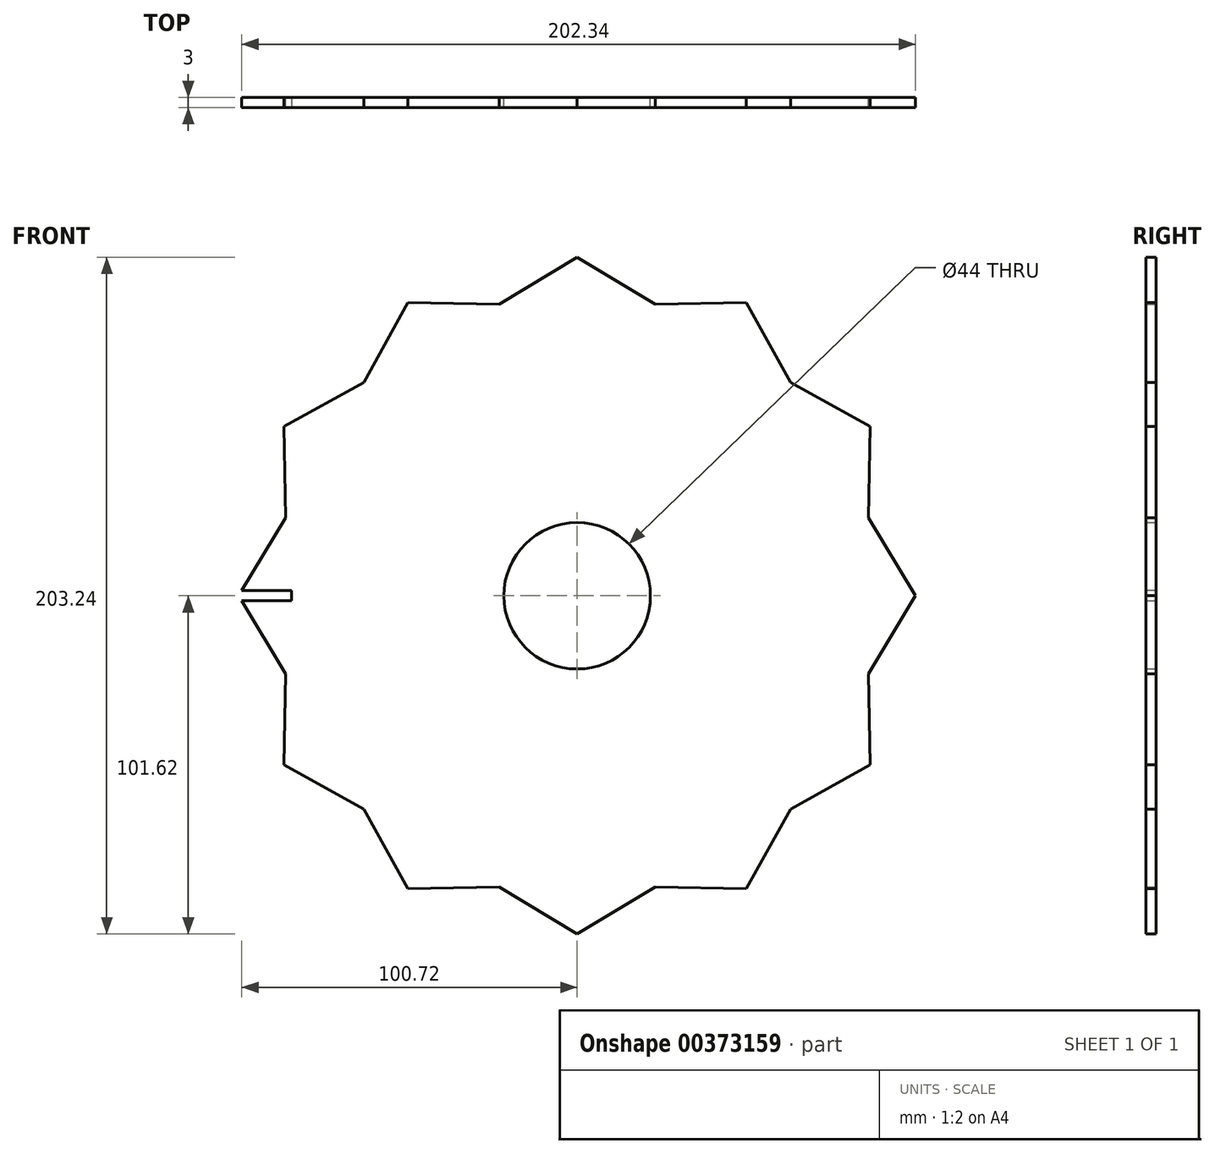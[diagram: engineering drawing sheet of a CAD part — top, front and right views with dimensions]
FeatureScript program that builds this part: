
annotation { "Feature Type Name" : "Feature", "Feature Type Description" : "" }
export const myFeature = defineFeature(function(context is Context, id is Id, definition is map)
    precondition{}
    {
        {
            var Q0;
            Q0=qCreatedBy(makeId("Front.planeOp"),FACE);
            var sketch = newSketch(context, id + "F0", { "sketchPlane" : qUnion([Q0])});
            skCircle(sketch, "E0", {"center": v(0, 0) * mm, "radius": 22 * mm});
            skLineSegment(sketch, "E1", {"start": v(-23.45, 87.53) * mm, "end": v(0, 101.62) * mm});
            skLineSegment(sketch, "E2", {"start": v(0, 101.62) * mm, "end": v(0, 56.8) * mm});
            skLineSegment(sketch, "E3.MirrorCS", {"start": v(23.45, 87.53) * mm, "end": v(0, 101.62) * mm});
            skLineSegment(sketch, "E4.1.0", {"start": v(-64.08, 64.08) * mm, "end": v(-50.81, 88) * mm});
            skLineSegment(sketch, "E4.1.1", {"start": v(-23.45, 87.53) * mm, "end": v(-50.81, 88) * mm});
            skLineSegment(sketch, "E4.2.0", {"start": v(-87.53, 23.45) * mm, "end": v(-88, 50.81) * mm});
            skLineSegment(sketch, "E4.2.1", {"start": v(-64.08, 64.08) * mm, "end": v(-88, 50.81) * mm});
            skLineSegment(sketch, "E4.3.0", {"start": v(-87.53, -23.45) * mm, "end": v(-101.62, 0) * mm});
            skLineSegment(sketch, "E4.3.1", {"start": v(-87.53, 23.45) * mm, "end": v(-101.62, 0) * mm});
            skLineSegment(sketch, "E4.4.1", {"start": v(-87.53, -23.45) * mm, "end": v(-88, -50.81) * mm});
            skLineSegment(sketch, "E4.5.0", {"start": v(-23.45, -87.53) * mm, "end": v(-50.81, -88) * mm});
            skLineSegment(sketch, "E4.5.1", {"start": v(-64.08, -64.08) * mm, "end": v(-50.81, -88) * mm});
            skLineSegment(sketch, "E4.6.0", {"start": v(23.45, -87.53) * mm, "end": v(0, -101.62) * mm});
            skLineSegment(sketch, "E4.6.1", {"start": v(-23.45, -87.53) * mm, "end": v(0, -101.62) * mm});
            skLineSegment(sketch, "E4.7.0", {"start": v(64.08, -64.08) * mm, "end": v(50.81, -88) * mm});
            skLineSegment(sketch, "E4.9.0", {"start": v(87.53, 23.45) * mm, "end": v(101.62, 0) * mm});
            skLineSegment(sketch, "E4.10.0", {"start": v(64.08, 64.08) * mm, "end": v(88, 50.81) * mm});
            skLineSegment(sketch, "E4.11.0", {"start": v(23.45, 87.53) * mm, "end": v(50.81, 88) * mm});
            skLineSegment(sketch, "E4.11.1", {"start": v(64.08, 64.08) * mm, "end": v(50.81, 88) * mm});
            skPoint(sketch, "E5.orphan", {"position": v(65.57, -60) * mm});
            skPoint(sketch, "E6.orphan", {"position": v(56.78, -32.78) * mm});
            skPoint(sketch, "E7.orphan", {"position": v(60, -65.57) * mm});
            skLineSegment(sketch, "E8.trimOffspring", {"start": v(64.08, -64.08) * mm, "end": v(88, -50.81) * mm});
            skPoint(sketch, "E9.orphan", {"position": v(84.75, -26.78) * mm});
            skLineSegment(sketch, "E10.trimOffspring", {"start": v(87.53, -23.45) * mm, "end": v(101.62, 0) * mm});
            skPoint(sketch, "E11.orphan", {"position": v(86.78, -19.18) * mm});
            skPoint(sketch, "E12.orphan", {"position": v(86.78, 19.18) * mm});
            skLineSegment(sketch, "E13.trimOffspring", {"start": v(87.53, 23.45) * mm, "end": v(88, 50.81) * mm});
            skPoint(sketch, "E14.orphan", {"position": v(65.57, 60) * mm});
            skPoint(sketch, "E15.orphan", {"position": v(84.75, 26.78) * mm});
            skPoint(sketch, "E16.orphan", {"position": v(56.78, 32.78) * mm});
            skPoint(sketch, "E17.orphan", {"position": v(60, 65.57) * mm});
            skPoint(sketch, "E18.MirrorCS.start.orphan", {"position": v(0, 65.57) * mm});
            skPoint(sketch, "E19.orphan", {"position": v(26.78, 84.75) * mm});
            skPoint(sketch, "E20.orphan", {"position": v(19.18, 86.78) * mm});
            skPoint(sketch, "E21.orphan", {"position": v(-19.18, 86.78) * mm});
            skPoint(sketch, "E22.orphan", {"position": v(-26.78, 84.75) * mm});
            skPoint(sketch, "E23.orphan", {"position": v(-60, 65.57) * mm});
            skPoint(sketch, "E24.orphan", {"position": v(-65.57, 60) * mm});
            skPoint(sketch, "E25.orphan", {"position": v(-32.78, 56.78) * mm});
            skPoint(sketch, "E26.orphan", {"position": v(-56.78, 32.78) * mm});
            skPoint(sketch, "E27.orphan", {"position": v(-86.78, 19.18) * mm});
            skPoint(sketch, "E28.orphan", {"position": v(-84.75, -26.78) * mm});
            skPoint(sketch, "E29.orphan", {"position": v(-65.57, -60) * mm});
            skPoint(sketch, "E30.orphan", {"position": v(-86.78, -19.18) * mm});
            skPoint(sketch, "E31.orphan", {"position": v(-60, -65.57) * mm});
            skLineSegment(sketch, "E32", {"start": v(87.53, -23.45) * mm, "end": v(88, -50.81) * mm});
            skLineSegment(sketch, "E33.trimOffspring", {"start": v(23.45, -87.53) * mm, "end": v(50.81, -88) * mm});
            skPoint(sketch, "E34.orphan", {"position": v(-19.18, -86.78) * mm});
            skPoint(sketch, "E35.orphan", {"position": v(19.18, -86.78) * mm});
            skLineSegment(sketch, "E36.trimOffspring", {"start": v(-64.08, -64.08) * mm, "end": v(-88, -50.81) * mm});
            skSolve(sketch);
        }
        {
            var Q0;
            Q0 = qSketchRegion(id + "F0", true);
            extrude(context, id + "F1", {"entities" : qUnion([Q0]), "depth" : 3 * mm});
        }
        {
            var Q0;
            Q0 = qSketchRegion(id + "F0", true);
            extrude(context, id + "F2", {"entities" : qUnion([Q0]), "operationType" : NewBodyOperationType.ADD, "depth" : 3 * mm});
        }
        {
            var Q0;
            Q0=makeQuery(id+"F1.opExtrude","CAP_FACE",FACE,{"disambiguationData":[OSD([sQuery(id+"F0.wireOp",EDGE,"E0"),sQuery(id+"F0.wireOp",EDGE,"E1"),sQuery(id+"F0.wireOp",EDGE,"E3.MirrorCS"),sQuery(id+"F0.wireOp",EDGE,"E4.1.0"),sQuery(id+"F0.wireOp",EDGE,"E4.1.1"),sQuery(id+"F0.wireOp",EDGE,"E4.2.0"),sQuery(id+"F0.wireOp",EDGE,"E4.2.1"),sQuery(id+"F0.wireOp",EDGE,"E4.3.0"),sQuery(id+"F0.wireOp",EDGE,"E4.3.1"),sQuery(id+"F0.wireOp",EDGE,"E4.4.1"),sQuery(id+"F0.wireOp",EDGE,"E4.5.0"),sQuery(id+"F0.wireOp",EDGE,"E4.5.1"),sQuery(id+"F0.wireOp",EDGE,"E4.6.0"),sQuery(id+"F0.wireOp",EDGE,"E4.6.1"),sQuery(id+"F0.wireOp",EDGE,"E4.7.0"),sQuery(id+"F0.wireOp",EDGE,"E4.9.0"),sQuery(id+"F0.wireOp",EDGE,"E4.10.0"),sQuery(id+"F0.wireOp",EDGE,"E4.11.0"),sQuery(id+"F0.wireOp",EDGE,"E4.11.1"),sQuery(id+"F0.wireOp",EDGE,"E8.trimOffspring"),sQuery(id+"F0.wireOp",EDGE,"E10.trimOffspring"),sQuery(id+"F0.wireOp",EDGE,"E13.trimOffspring"),sQuery(id+"F0.wireOp",EDGE,"E32"),sQuery(id+"F0.wireOp",EDGE,"E33.trimOffspring"),sQuery(id+"F0.wireOp",EDGE,"E36.trimOffspring")])],"isStart":false});
            var sketch = newSketch(context, id + "F3", { "sketchPlane" : qUnion([Q0])});
            skLineSegment(sketch, "E37.bottom", {"start": v(-85.72, 1.5) * mm, "end": v(-100.72, 1.5) * mm});
            skLineSegment(sketch, "E37.top", {"start": v(-85.72, -1.5) * mm, "end": v(-100.72, -1.5) * mm});
            skLineSegment(sketch, "E37.left", {"start": v(-85.72, 1.5) * mm, "end": v(-85.72, -1.5) * mm});
            skPoint(sketch, "E37.middle", {"position": v(-101.62, 0) * mm});
            skPoint(sketch, "E38", {"position": v(-100.72, -1.5) * mm});
            skPoint(sketch, "E39", {"position": v(-100.72, 1.5) * mm});
            skPoint(sketch, "E40.orphan", {"position": v(-117.53, -1.5) * mm});
            skPoint(sketch, "E41.orphan", {"position": v(-117.53, 1.5) * mm});
            skLineSegment(sketch, "E42.bottom", {"start": v(-100.72, 1.5) * mm, "end": v(-100.72, 1.5) * mm});
            skLineSegment(sketch, "E42.top", {"start": v(-100.72, -4.5) * mm, "end": v(-100.72, -4.5) * mm});
            skLineSegment(sketch, "E43.bottom", {"start": v(-100.72, -1.5) * mm, "end": v(-117.5, -1.5) * mm});
            skLineSegment(sketch, "E43.top", {"start": v(-100.72, 14) * mm, "end": v(-117.5, 14) * mm});
            skLineSegment(sketch, "E43.left", {"start": v(-100.72, 1.5) * mm, "end": v(-100.72, 14) * mm});
            skLineSegment(sketch, "E43.right", {"start": v(-117.5, -1.5) * mm, "end": v(-117.5, 14) * mm});
            skSolve(sketch);
        }
        {
            var Q0;
            Q0 = qSketchRegion(id + "F3", true);
            extrude(context, id + "F4", {"entities" : qUnion([Q0]), "operationType" : NewBodyOperationType.REMOVE, "oppositeDirection" : true, "depth" : 25 * mm});
        }
    });
